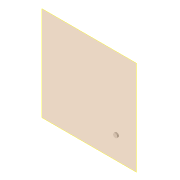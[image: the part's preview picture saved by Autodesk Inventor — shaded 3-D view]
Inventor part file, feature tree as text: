
AUTODESK INVENTOR PART (.ipt)
format: ipt  version: 2022 (Build 260153000, 153)  size: 81,920 bytes
history: native  units: mm
features: other x2, plane x1, extrude x1, sketch x1, reference x1
ambient origin geometry x8: Origin, YZ Plane, XZ Plane, XY Plane, X Axis, Y Axis, Z Axis, Center Point
bodies: Volumenkörper1 (feature_tree)
feature tree (6):
  plane  "Arbeitsebene1"
  extrude  "Extrusion1"  Depth=3.0mm TaperAngle=0.0deg
  sketch  "Skizze1"  dims[d0=8.0mm d1=3.0mm d2=0.0mm]
  reference  "Referenz1"
  other  "Assembly_XYTable_Aliexpress_Housing.iam"
  other  "30_XYTable_Aliexpress_Baseplate_aluminium_CNC:1"
